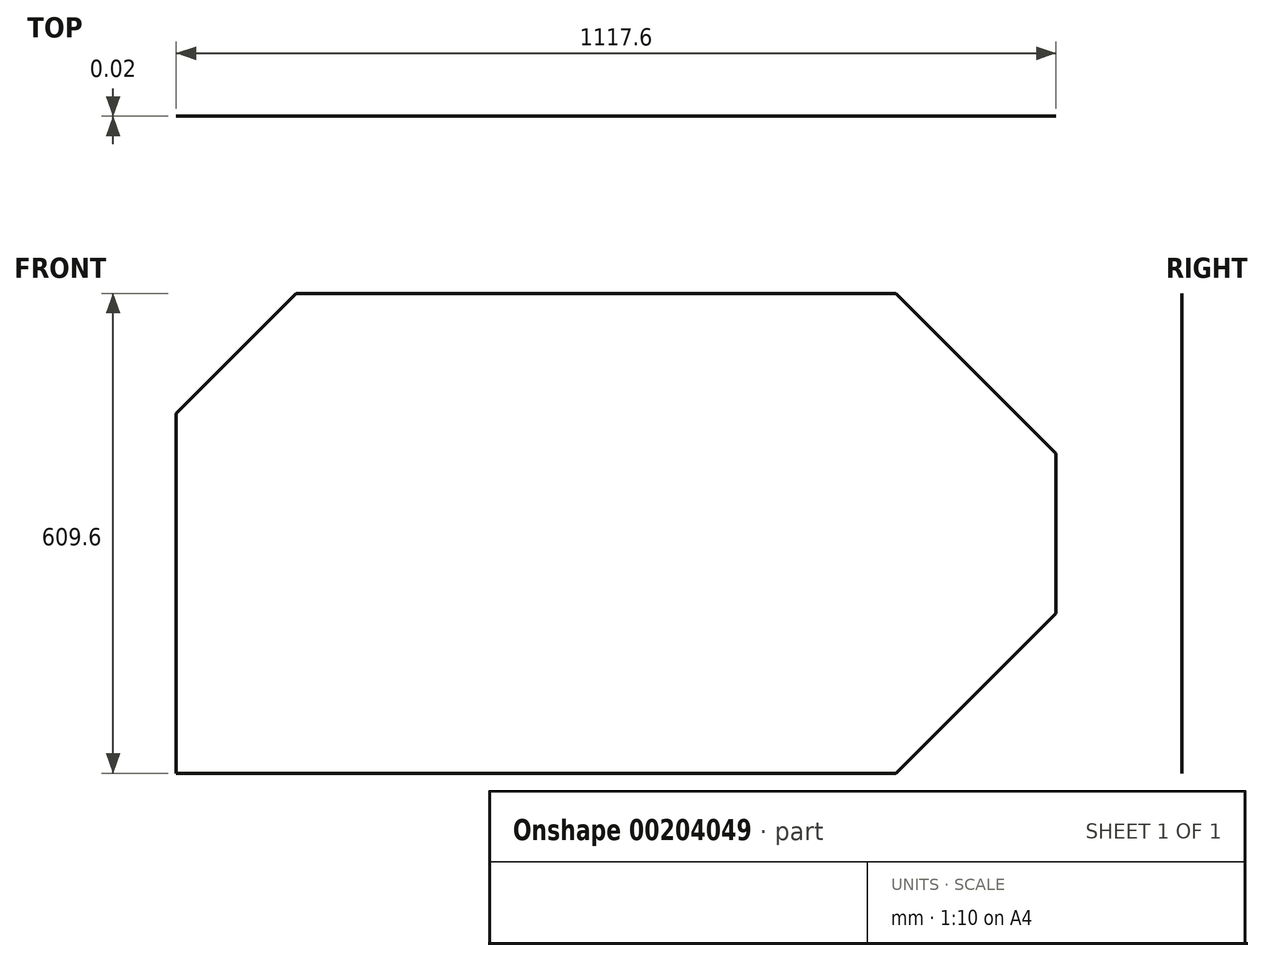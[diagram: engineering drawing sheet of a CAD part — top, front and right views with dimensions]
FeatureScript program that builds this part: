
annotation { "Feature Type Name" : "Feature", "Feature Type Description" : "" }
export const myFeature = defineFeature(function(context is Context, id is Id, definition is map)
    precondition{}
    {
        {
            var Q0;
            Q0=qCreatedBy(makeId("Front.planeOp"),FACE);
            var sketch = newSketch(context, id + "F0", { "sketchPlane" : qUnion([Q0])});
            skLineSegment(sketch, "E0", {"start": v(0, 0) * mm, "end": v(0, 457.2) * mm});
            skLineSegment(sketch, "E1", {"start": v(152.4, 609.6) * mm, "end": v(0, 457.2) * mm});
            skLineSegment(sketch, "E2", {"start": v(0, 0) * mm, "end": v(914.4, 0) * mm});
            skLineSegment(sketch, "E3", {"start": v(1117.6, 203.2) * mm, "end": v(1117.6, 406.4) * mm});
            skLineSegment(sketch, "E4", {"start": v(914.4, 609.6) * mm, "end": v(1117.6, 406.4) * mm});
            skLineSegment(sketch, "E5", {"start": v(1117.6, 203.2) * mm, "end": v(914.4, 0) * mm});
            skLineSegment(sketch, "E6", {"start": v(152.4, 609.6) * mm, "end": v(914.4, 609.6) * mm});
            skPoint(sketch, "E7.start.orphan", {"position": v(0, 609.6) * mm});
            skPoint(sketch, "E8.orphan", {"position": v(1117.6, 609.6) * mm});
            skPoint(sketch, "E9.orphan", {"position": v(1117.6, 0) * mm});
            skSolve(sketch);
        }
        {
            var Q0;
            Q0=makeQuery(id+"F0.imprint","IMPRINT",FACE,{"disambiguationData":[TD([[makeQuery(id+"F0.imprint","IMPRINT",EDGE,{"derivedFrom":sQuery(id+"F0.wireOp",EDGE,"E0")}),-1.0]])]});
            extrude(context, id + "F1", {"entities" : qUnion([Q0]), "endBound" : BoundingType.SYMMETRIC, "depth" : ((1 / 12) / 4) * mm});
        }
    });
